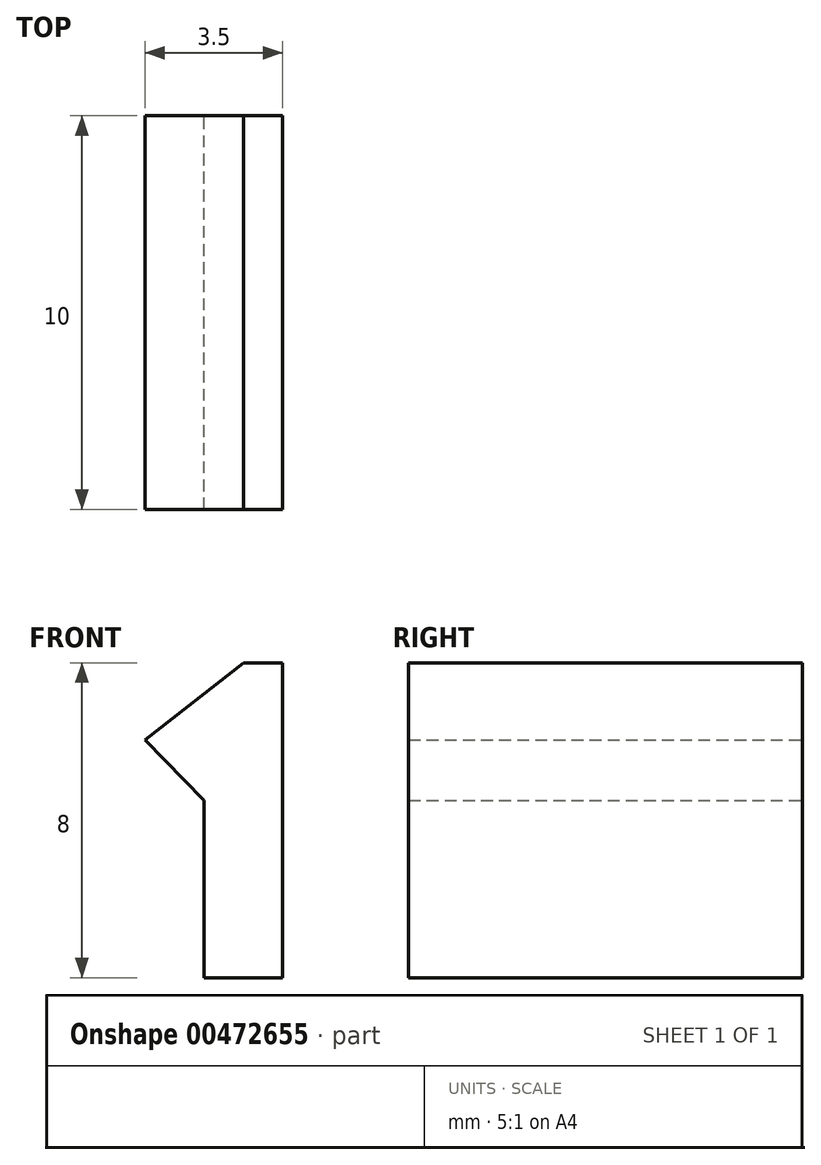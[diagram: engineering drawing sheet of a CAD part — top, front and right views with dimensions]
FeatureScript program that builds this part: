
annotation { "Feature Type Name" : "Feature", "Feature Type Description" : "" }
export const myFeature = defineFeature(function(context is Context, id is Id, definition is map)
    precondition{}
    {
        {
            var Q0;
            Q0=qCreatedBy(makeId("Front.planeOp"),FACE);
            var sketch = newSketch(context, id + "F0", { "sketchPlane" : qUnion([Q0])});
            skLineSegment(sketch, "E0", {"start": v(0, 0) * mm, "end": v(0, 8) * mm});
            skLineSegment(sketch, "E1", {"start": v(0, 8) * mm, "end": v(-1, 8) * mm});
            skLineSegment(sketch, "E2", {"start": v(-1, 8) * mm, "end": v(-3.5, 6.04) * mm});
            skLineSegment(sketch, "E3", {"start": v(-3.5, 6.04) * mm, "end": v(-2, 4.5) * mm});
            skLineSegment(sketch, "E4", {"start": v(-2, 4.5) * mm, "end": v(-2, 0) * mm});
            skLineSegment(sketch, "E5", {"start": v(-2, 0) * mm, "end": v(0, 0) * mm});
            skSolve(sketch);
        }
        {
            var Q0;
            Q0 = qSketchRegion(id + "F0", true);
            var Q1;
            Q1=makeQuery(id+"F0.imprint","IMPRINT",FACE,{"disambiguationData":[TD([[makeQuery(id+"F0.imprint","IMPRINT",EDGE,{"derivedFrom":sQuery(id+"F0.wireOp",EDGE,"E0")}),1.0]])]});
            extrude(context, id + "F1", {"entities" : qUnion([Q0, Q1]), "depth" : 10 * mm});
        }
    });
